# Revit family: Resideo_ThermostaticRadiatorValve_V2100Ezzz
name_source: partatom
category: Pipe Accessories
units: mm (PartAtom-declared; Revit-internal decimal feet)

## family parameters
Always vertical = Yes
Cut with Voids When Loaded = No
OmniClass Number = 23.65.55.00
OmniClass Title = Distribution of Supplied Liquids/Gases
Part Type = Valve - Breaks Into
Round Connector Dimension = Use Radius
Shared = No
Work Plane-Based = No

## types (3) — shared parameters
AmbientTemperature = 0 ... 40 °C
Approvals = EN215
Assembly Code = D20
AssetType = Fixed
BIMObjectName = Resideo_ThermostaticRadiatorValve_V2100E
ClassificationName = Uniclass 2015
ClassificationValue = Pr_65_54_95_89
ClosingDimension = 11.5 mm
ConnectionType = M30x1.5
Description = PI-TRV BODY ANGLE
DifferentialPressure = 0.1 … 0.6 bar
DocumentationCertificates = https://www.bimstore.co
DocumentationInstallationGuide = https://www.bimstore.co
DocumentationLiterature = https://www.bimstore.co
DocumentationMaintenance = https://www.bimstore.co
DocumentationTechnical = https://www.bimstore.co
DurationUnit = Year
FlowController = Yes
Force = 90 Nm
IfcExportAs = IfcValve
IfcExportType = IfcValveTypeEnum.ISOLATING
Keynote = S
Loss Method = K Coefficient
Manufacturer = Resideo
ManufacturerName = Resideo
Material = Brass
MaximumAmbientRelativeHumidity = 75 % (non condensing)
MaximumFlow = 2.7 L/min
MaximumOperatingPressure = 10.0 bar
MediaTemperatureRange = 2 ... 90 °C
MediumType = Water or water-glycol mixture according to VDI 2035
MinimumFlow = 0.2 L/min
ModelReference = PI-TRV BODY ANGLE
NBSDescription = Thermostatic radiator valves
NBSObjectName = Resideo - Thermostatic radiator valves
NBSReference = 90-10-90/364
NominalFlow = 120 kg/h
NominalPressure = PN10
PreSetting = Yes
PrimaryMaterial = Resideo - Brass - Nickel Plated
ProductionYear = 2023
SecondaryMaterial = Resideo - Plastic - Blue
StrokeStandard = 2.5 mm
Type Comments = PI-TRV BODY ANGLE
URL = www.resideo.com
ValveSeries = V2100, Kombi-TRV
ValveType = V2100E
WarrantyDurationLabor = 0
WarrantyDurationParts = 0
WarrantyDurationUnit = Year
WarrantyGuarantorLabor = www.resideo.com/gb/en/contact-us/
WarrantyGuarantorParts = www.resideo.com/gb/en/contact-us/
_BSBibleVersion = 16
_CurrentRevision = 1
_DistributedBy = https://www.bimstore.co
_ObjectUserGuide = https://www.bimstore.co
pH-Range = 8 ... 9.5
zero-valued in all types: Cost, Default Elevation, ExpectedLife, K Coefficient, _BimSpecGuid

## per-type parameters (varying)
| type | BodyOffset | ConnectionRadius | ConnectionSize | DN10 | DN15 | DN20 | NominalDepth | NominalHeight | NominalLength | PipeConnection | RadiatorConnection | Size | a | b | c | d |
| V2100EPI10 | 23.7 mm | 5 mm  [stored 0.0164042 ft] | 10 mm  [stored 0.0328084 ft] | Yes | No | No | 35 mm | 68 mm | 51 mm | Rp 3/8" | R 3/8" | 51mm (L) x 68mm (H) x 35mm (D) | 22 mm  [stored 0.0721785 ft] | 32.8 mm  [stored 0.107612 ft] | 15 mm  [stored 0.0492126 ft] | 7 mm  [stored 0.0229659 ft] |
| V2100EPI15 | 25.2 mm | 7.5 mm | 15 mm  [stored 0.0492126 ft] | No | Yes | No | 35 mm | 74 mm | 53 mm | Rp 1/2" | R 1/2" | 53mm (L) x 74mm (H) x 35mm (D) | 26 mm | 35.3 mm | 20 mm  [stored 0.0656168 ft] | 10 mm  [stored 0.0328084 ft] |
| V2100EPI20 | 21.7 mm | 10 mm  [stored 0.0328084 ft] | 20 mm  [stored 0.0656168 ft] | No | No | Yes | 43 mm | 73 mm | 59 mm | Rp 3/4" | R 3/4" | 59mm (L) x 73mm (H) x 43mm (D) | 29 mm | 40.4 mm | 25 mm  [stored 0.082021 ft] | 13 mm |

note: column(s) folded — value = type name in every type: Model, ModelNumber, TypeName

note: [stored X ft] marks values corroborated as IEEE doubles in the binary element streams (Revit-internal decimal feet)

## geometry (parser evidence)
native form markers: Sweep x2
no freeform markers — native parametric forms only
